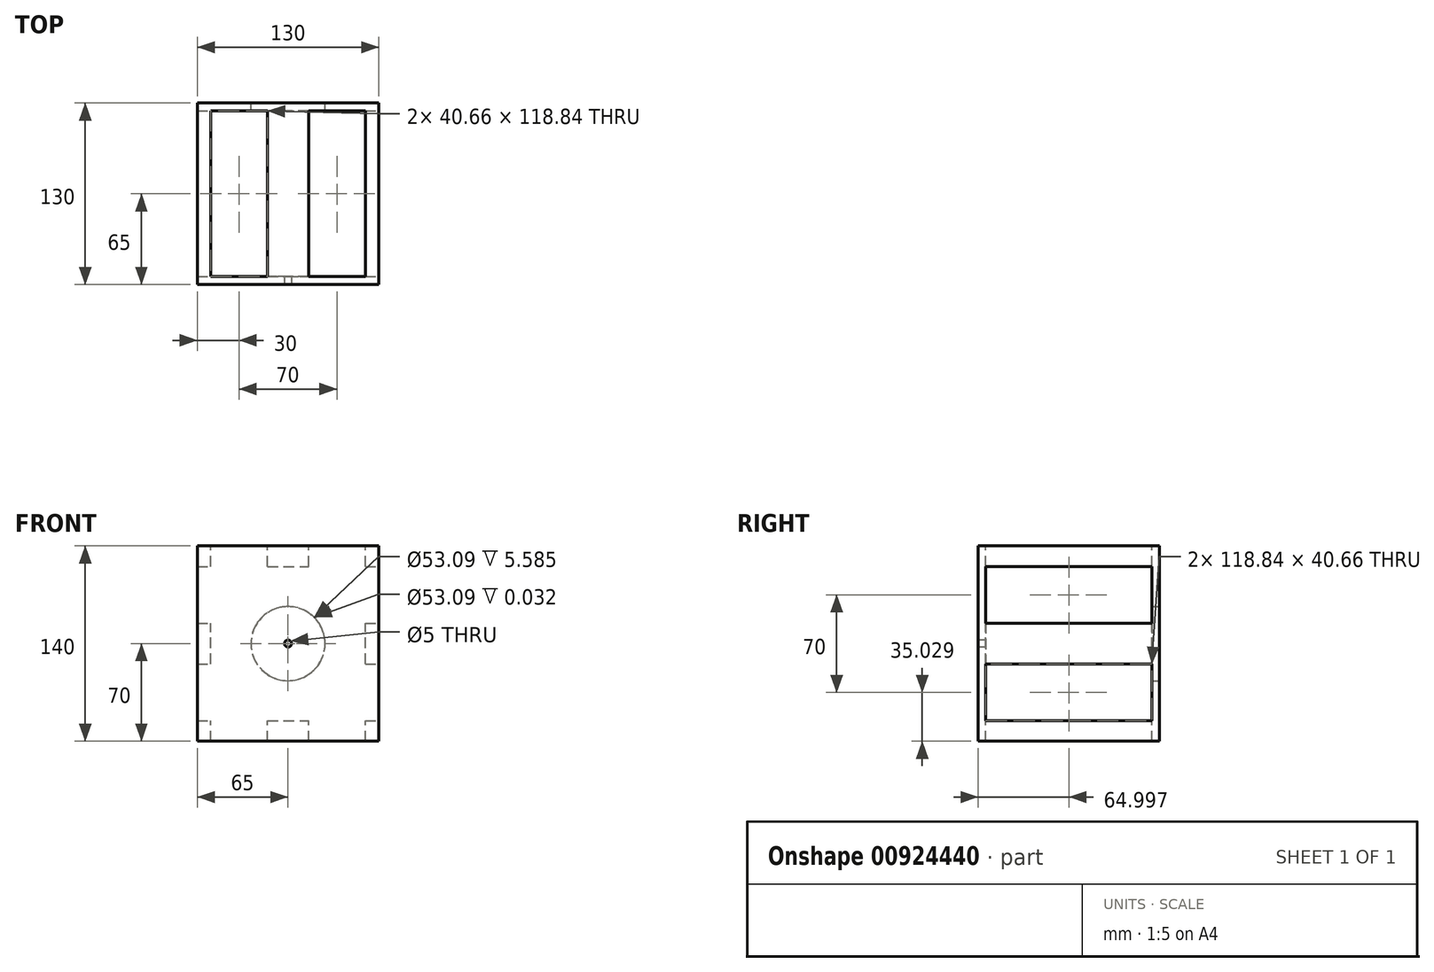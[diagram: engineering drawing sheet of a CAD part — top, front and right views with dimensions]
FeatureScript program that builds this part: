
annotation { "Feature Type Name" : "Feature", "Feature Type Description" : "" }
export const myFeature = defineFeature(function(context is Context, id is Id, definition is map)
    precondition{}
    {
        {
            var Q0;
            Q0=qCreatedBy(makeId("Front.planeOp"),FACE);
            var sketch = newSketch(context, id + "F0", { "sketchPlane" : qUnion([Q0])});
            skLineSegment(sketch, "E0.bottom", {"start": v(-65, 70) * mm, "end": v(65, 70) * mm});
            skLineSegment(sketch, "E0.top", {"start": v(-65, -70) * mm, "end": v(65, -70) * mm});
            skLineSegment(sketch, "E0.left", {"start": v(-65, 70) * mm, "end": v(-65, -70) * mm});
            skLineSegment(sketch, "E0.right", {"start": v(65, 70) * mm, "end": v(65, -70) * mm});
            skPoint(sketch, "E0.middle", {"position": v(0, 0) * mm});
            skSolve(sketch);
        }
        {
            var Q0;
            Q0=qSketchRegion(id+"F0",true);
            extrude(context, id + "F1", {"entities" : qUnion([Q0]), "depth" : 130 * mm, "offsetDistance" : 25 * mm});
        }
        {
            var Q0;
            Q0=makeQuery(id+"F1.opExtrude","CAP_FACE",FACE,{"disambiguationData":[OSD([sQuery(id+"F0.wireOp",EDGE,"E0.bottom"),sQuery(id+"F0.wireOp",EDGE,"E0.top"),sQuery(id+"F0.wireOp",EDGE,"E0.left"),sQuery(id+"F0.wireOp",EDGE,"E0.right")])],"isStart":true});
            var sketch = newSketch(context, id + "F2", { "sketchPlane" : qUnion([Q0])});
            skCircle(sketch, "E1", {"center": v(0, 0) * mm, "radius": 26.55 * mm});
            skSolve(sketch);
        }
        {
            var Q0;
            Q0=makeQuery(id+"F2.imprint","IMPRINT",FACE,{"disambiguationData":[TD([[makeQuery(id+"F2.imprint","IMPRINT",EDGE,{"derivedFrom":sQuery(id+"F2.wireOp",EDGE,"E1")}),1.0]])]});
            extrude(context, id + "F3", {"entities" : qUnion([Q0]), "operationType" : NewBodyOperationType.REMOVE, "oppositeDirection" : true, "depth" : 124.45 * mm, "offsetDistance" : 25 * mm});
        }
        {
            var Q0;
            Q0=makeQuery(id+"F1.opExtrude","SWEPT_FACE",FACE,{"disambiguationData":[OSD([sQuery(id+"F0.wireOp",EDGE,"E0.bottom")])]});
            var sketch = newSketch(context, id + "F4", { "sketchPlane" : qUnion([Q0])});
            skLineSegment(sketch, "E2", {"start": v(0, 0) * mm, "end": v(0, -130) * mm});
            skLineSegment(sketch, "E3.bottom", {"start": v(-55.33, -5.58) * mm, "end": v(-14.67, -5.58) * mm});
            skLineSegment(sketch, "E3.top", {"start": v(-55.33, -124.42) * mm, "end": v(-14.67, -124.42) * mm});
            skLineSegment(sketch, "E3.left", {"start": v(-55.33, -5.58) * mm, "end": v(-55.33, -124.42) * mm});
            skLineSegment(sketch, "E3.right", {"start": v(-14.67, -5.58) * mm, "end": v(-14.67, -124.42) * mm});
            skPoint(sketch, "E3.middle", {"position": v(-35, -65) * mm});
            skLineSegment(sketch, "E4.MirrorCS", {"start": v(14.67, -5.58) * mm, "end": v(14.67, -124.42) * mm});
            skLineSegment(sketch, "E5.MirrorCS", {"start": v(55.33, -5.58) * mm, "end": v(14.67, -5.58) * mm});
            skLineSegment(sketch, "E6.MirrorCS", {"start": v(55.33, -5.58) * mm, "end": v(55.33, -124.42) * mm});
            skLineSegment(sketch, "E7.MirrorCS", {"start": v(55.33, -124.42) * mm, "end": v(14.67, -124.42) * mm});
            skSolve(sketch);
        }
        {
            var Q0;
            Q0=makeQuery(id+"F4.imprint","IMPRINT",FACE,{"disambiguationData":[TD([[makeQuery(id+"F4.imprint","IMPRINT",EDGE,{"derivedFrom":sQuery(id+"F4.wireOp",EDGE,"2921cbc2-2453-4714-a8a2-5baeffaab715.bottom")}),-1.0]])]});
            var Q1;
            Q1=makeQuery(id+"F4.imprint","IMPRINT",FACE,{"disambiguationData":[TD([[makeQuery(id+"F4.imprint","IMPRINT",EDGE,{"derivedFrom":sQuery(id+"F4.wireOp",EDGE,"3097a6d6-c18d-4542-bddb-5d9b6566663d0.MirrorCS")}),-1.0]])]});
            var Q2;
            Q2=makeQuery(id+"F4.imprint","IMPRINT",FACE,{"disambiguationData":[TD([[makeQuery(id+"F4.imprint","IMPRINT",EDGE,{"derivedFrom":sQuery(id+"F4.wireOp",EDGE,"E3.bottom")}),-1.0]])]});
            var Q3;
            Q3=makeQuery(id+"F4.imprint","IMPRINT",FACE,{"disambiguationData":[TD([[makeQuery(id+"F4.imprint","IMPRINT",EDGE,{"derivedFrom":sQuery(id+"F4.wireOp",EDGE,"E4.MirrorCS")}),1.0]])]});
            extrude(context, id + "F5", {"entities" : qUnion([Q0, Q1, Q2, Q3]), "operationType" : NewBodyOperationType.REMOVE, "oppositeDirection" : true, "depth" : 140 * mm, "offsetDistance" : 25 * mm});
        }
        {
            var Q0;
            Q0=makeQuery(id+"F1.opExtrude","SWEPT_FACE",FACE,{"disambiguationData":[OSD([sQuery(id+"F0.wireOp",EDGE,"E0.right")])]});
            var sketch = newSketch(context, id + "F6", { "sketchPlane" : qUnion([Q0])});
            skLineSegment(sketch, "E8", {"start": v(0, 0.03) * mm, "end": v(-130, 0.03) * mm});
            skLineSegment(sketch, "E9.bottom", {"start": v(-5.58, 55.36) * mm, "end": v(-5.58, 14.7) * mm});
            skLineSegment(sketch, "E9.top", {"start": v(-124.42, 55.36) * mm, "end": v(-124.42, 14.7) * mm});
            skLineSegment(sketch, "E9.left", {"start": v(-5.58, 55.36) * mm, "end": v(-124.42, 55.36) * mm});
            skLineSegment(sketch, "E9.right", {"start": v(-5.58, 14.7) * mm, "end": v(-124.42, 14.7) * mm});
            skLineSegment(sketch, "E10.MirrorCS", {"start": v(-5.58, -14.64) * mm, "end": v(-124.42, -14.64) * mm});
            skLineSegment(sketch, "E11.MirrorCS", {"start": v(-5.58, -55.3) * mm, "end": v(-5.58, -14.64) * mm});
            skLineSegment(sketch, "E12.MirrorCS", {"start": v(-5.58, -55.3) * mm, "end": v(-124.42, -55.3) * mm});
            skLineSegment(sketch, "E13.MirrorCS", {"start": v(-124.42, -55.3) * mm, "end": v(-124.42, -14.64) * mm});
            skSolve(sketch);
        }
        {
            var Q0;
            Q0=makeQuery(id+"F6.imprint","IMPRINT",FACE,{"disambiguationData":[TD([[makeQuery(id+"F6.imprint","IMPRINT",EDGE,{"derivedFrom":sQuery(id+"F6.wireOp",EDGE,"ee195015-2383-4ffa-83cd-e6111870ca52.MirrorCS")}),-1.0]])]});
            var Q1;
            Q1=makeQuery(id+"F6.imprint","IMPRINT",FACE,{"disambiguationData":[TD([[makeQuery(id+"F6.imprint","IMPRINT",EDGE,{"derivedFrom":sQuery(id+"F6.wireOp",EDGE,"ebd0df40-f740-42c3-bd54-c1f5c1fb7ffd.bottom")}),-1.0]])]});
            var Q2;
            Q2=makeQuery(id+"F6.imprint","IMPRINT",FACE,{"disambiguationData":[TD([[makeQuery(id+"F6.imprint","IMPRINT",EDGE,{"derivedFrom":sQuery(id+"F6.wireOp",EDGE,"E9.bottom")}),-1.0]])]});
            var Q3;
            Q3=makeQuery(id+"F6.imprint","IMPRINT",FACE,{"disambiguationData":[TD([[makeQuery(id+"F6.imprint","IMPRINT",EDGE,{"derivedFrom":sQuery(id+"F6.wireOp",EDGE,"E10.MirrorCS")}),1.0]])]});
            extrude(context, id + "F7", {"entities" : qUnion([Q0, Q1, Q2, Q3]), "operationType" : NewBodyOperationType.REMOVE, "oppositeDirection" : true, "depth" : 140 * mm, "offsetDistance" : 25 * mm});
        }
        {
            var Q0;
            Q0=makeQuery(id+"F1.opExtrude","CAP_FACE",FACE,{"disambiguationData":[OSD([sQuery(id+"F0.wireOp",EDGE,"E0.bottom"),sQuery(id+"F0.wireOp",EDGE,"E0.top"),sQuery(id+"F0.wireOp",EDGE,"E0.left"),sQuery(id+"F0.wireOp",EDGE,"E0.right")])],"isStart":false});
            var sketch = newSketch(context, id + "F8", { "sketchPlane" : qUnion([Q0])});
            skCircle(sketch, "E14", {"center": v(0, 0) * mm, "radius": 2.5 * mm});
            skSolve(sketch);
        }
        {
            var Q0;
            Q0=qSketchRegion(id+"F8",true);
            extrude(context, id + "F9", {"entities" : qUnion([Q0]), "operationType" : NewBodyOperationType.REMOVE, "oppositeDirection" : true, "depth" : 7.6 * mm, "offsetDistance" : 25 * mm});
        }
    });
